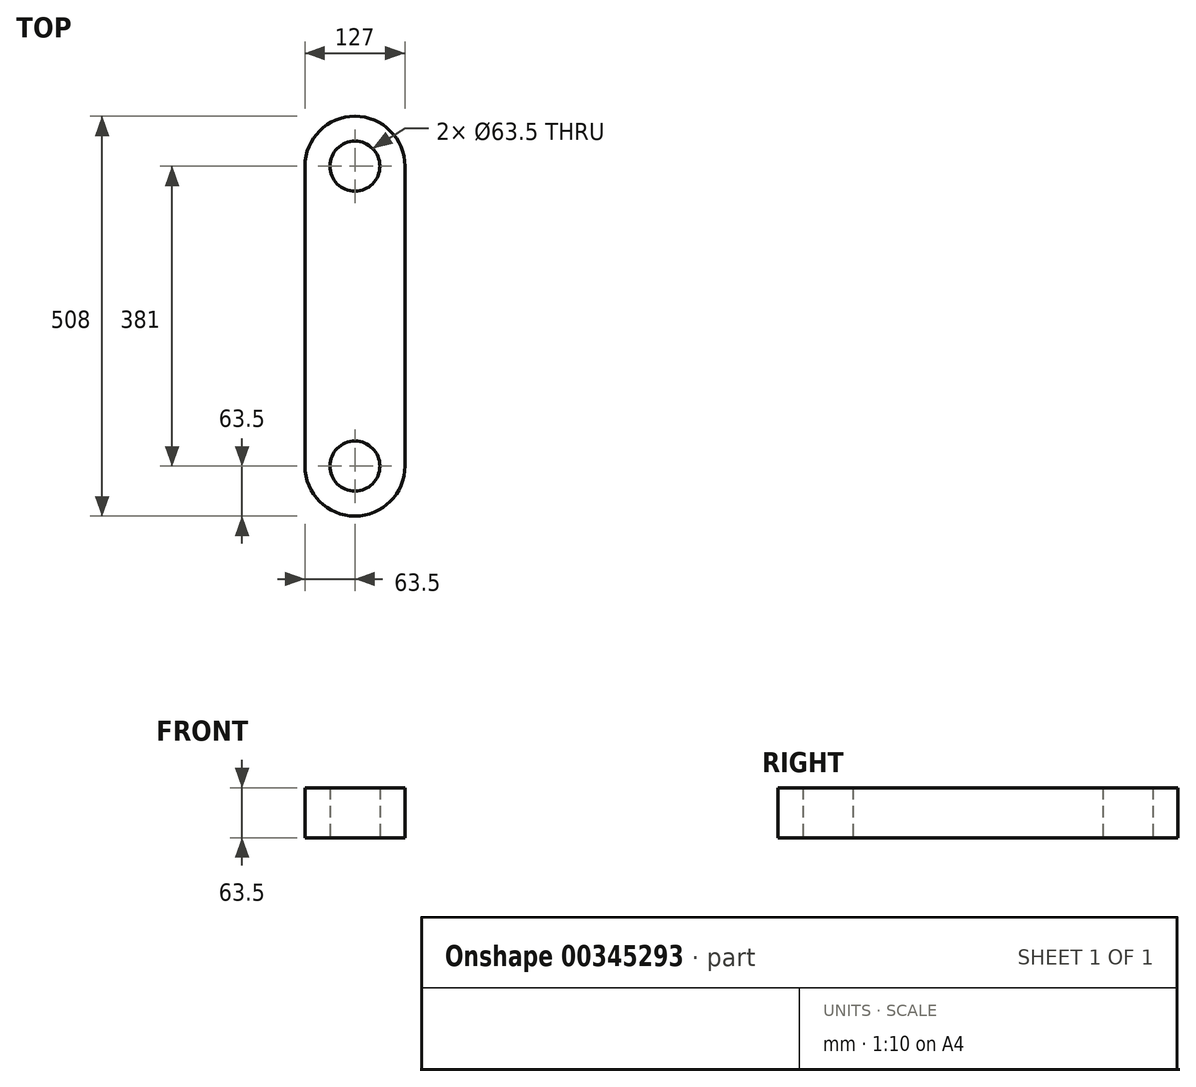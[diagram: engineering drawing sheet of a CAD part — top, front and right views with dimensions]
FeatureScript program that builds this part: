
annotation { "Feature Type Name" : "Feature", "Feature Type Description" : "" }
export const myFeature = defineFeature(function(context is Context, id is Id, definition is map)
    precondition{}
    {
        {
            var Q0;
            Q0=qCreatedBy(makeId("Top.planeOp"),FACE);
            var sketch = newSketch(context, id + "F0", { "sketchPlane" : qUnion([Q0])});
            skLineSegment(sketch, "E0.bottom", {"start": v(63.5, -190.5) * mm, "end": v(-63.5, -190.5) * mm});
            skLineSegment(sketch, "E0.top", {"start": v(63.5, 190.5) * mm, "end": v(-63.5, 190.5) * mm});
            skLineSegment(sketch, "E0.left", {"start": v(63.5, -190.5) * mm, "end": v(63.5, 190.5) * mm});
            skLineSegment(sketch, "E0.right", {"start": v(-63.5, -190.5) * mm, "end": v(-63.5, 190.5) * mm});
            skPoint(sketch, "E0.middle", {"position": v(0, 0) * mm});
            skCircle(sketch, "E1", {"center": v(0, 190.5) * mm, "radius": 63.5 * mm});
            skCircle(sketch, "E2", {"center": v(0, -190.5) * mm, "radius": 63.5 * mm});
            skSolve(sketch);
        }
        {
            var Q0;
            Q0 = qSketchRegion(id + "F0", true);
            extrude(context, id + "F1", {"entities" : qUnion([Q0]), "depth" : 63.5 * mm});
        }
        {
            var Q0;
            Q0=qCreatedBy(makeId("Top.planeOp"),FACE);
            var sketch = newSketch(context, id + "F2", { "sketchPlane" : qUnion([Q0])});
            skCircle(sketch, "E3", {"center": v(0, 190.5) * mm, "radius": 31.75 * mm});
            skCircle(sketch, "E4", {"center": v(0, -190.5) * mm, "radius": 31.75 * mm});
            skSolve(sketch);
        }
        {
            var Q0;
            Q0 = qSketchRegion(id + "F2", true);
            var Q1;
            Q1=makeQuery(id+"F1.opExtrude","SWEPT_BODY",BODY,{"disambiguationData":[OSD([sQuery(id+"F0.wireOp",EDGE,"E0.left"),sQuery(id+"F0.wireOp",EDGE,"E0.right"),sQuery(id+"F0.wireOp",EDGE,"E1"),sQuery(id+"F0.wireOp",EDGE,"E2")])]});
            extrude(context, id + "F3", {"entities" : qUnion([Q0]), "operationType" : NewBodyOperationType.REMOVE, "endBound" : BoundingType.UP_TO_BODY, "endBoundEntityBody" : qUnion([Q1]), "depth" : 25.4 * mm});
        }
    });
